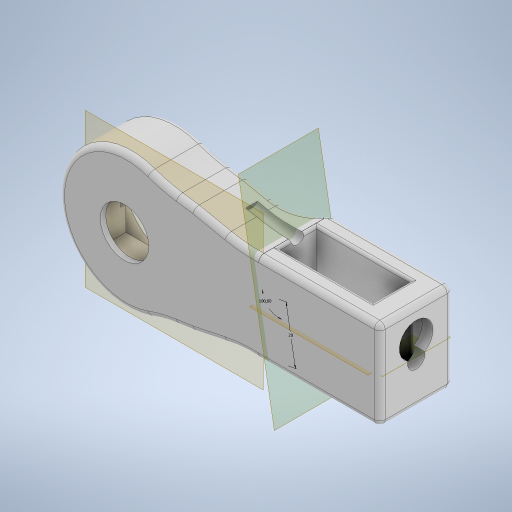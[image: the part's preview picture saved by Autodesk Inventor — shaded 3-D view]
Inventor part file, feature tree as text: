
AUTODESK INVENTOR PART (.ipt)
format: ipt  version: 2024 (Build 280153000, 153)  size: 3,128,320 bytes
history: native  units: mm
features: extrude x13, projected_geometry x9, plane x6, fillet x6, other x6, mirror x3, reference x3
ambient origin geometry x8: Origin, YZ Plane, XZ Plane, XY Plane, X Axis, Y Axis, Z Axis, Center Point
bodies: Solid1 (feature_tree)
feature tree (46):
  plane  "Work Plane1"
  extrude  "Extrusion1"  Depth=40.25mm
  extrude  "Extrusion2"  Depth=20.25mm
  plane  "Work Plane2"
  extrude  "Extrusion3"  TaperAngle=0.0deg  [1 undecoded]
  mirror  "Mirror2"
  extrude  "Extrusion4"  Depth=40.25mm
  extrude  "Extrusion6"  Depth=50.0mm
  fillet  "Fillet1"  Radius=49.05mm
  extrude  "Extrusion7"  Depth=15.0mm
  extrude  "Extrusion8"  Depth=15.0mm
  extrude  "Extrusion9"  Depth=20.0mm
  extrude  "Extrusion10"  Depth=20.0mm
  plane  "Work Plane3"
  fillet  "Fillet7"  Radius=12.817996mm
  fillet  "Fillet8"  Radius=12.817996mm
  fillet  "Fillet10"  Radius=8.0mm
  extrude  "Extrusion12"  Depth=10.125mm
  fillet  "Fillet15"  Radius=5.5mm
  extrude  "Extrusion13"  Depth=1.0mm
  fillet  "Fillet16"  Radius=1.0mm
  extrude  "Extrusion15"  Depth=2.0mm TaperAngle=0.0deg
  plane  "Work Plane7"
  extrude  "Extrusion17"  Depth=20.5mm
  plane  "Work Plane8"
  mirror  "Mirror4"
  plane  "Work Plane9"
  mirror  "Mirror5"
  reference  "Reference1"
  reference  "Reference2"
  reference  "Reference3"
  projected_geometry  "Projected Loop1"
  projected_geometry  "Projected Loop2"
  projected_geometry  "Projected Loop3"
  projected_geometry  "Projected Loop5"
  projected_geometry  "Projected Loop7"
  projected_geometry  "Projected Loop8"
  projected_geometry  "Projected Loop10"
  projected_geometry  "Projected Loop12"
  projected_geometry  "Projected Loop14"
  other  "<userpath> windows\Documents\Inventor\Robotska_roka\Assembly4.iam"
  other  "Assembly4.iam"
  other  "Servo Motor MG996R  With Attachments:5"
  other  "servoMotorMG996R_7"
  other  "Servo Motor MG996R  With Attachments:6"
  other  "attachmentCircular_1"
note: 1 required parameter value undecoded (feature->parameter linkage not recoverable at this tier; creation-order binding heuristic only, values carry confidence <= 0.55)
